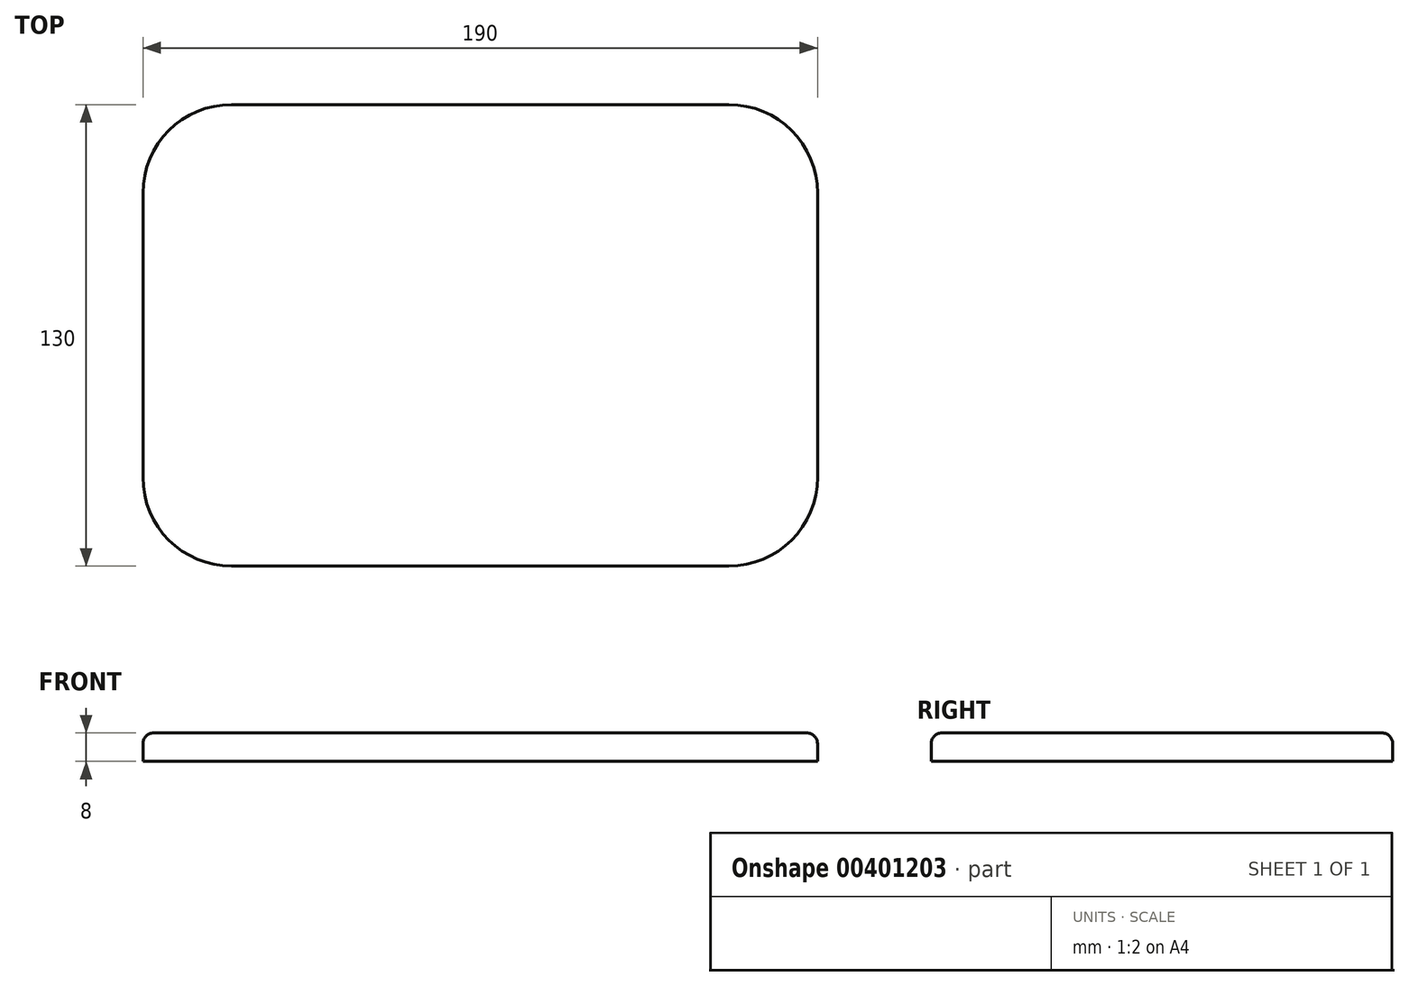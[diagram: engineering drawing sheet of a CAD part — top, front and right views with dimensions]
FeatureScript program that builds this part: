
annotation { "Feature Type Name" : "Feature", "Feature Type Description" : "" }
export const myFeature = defineFeature(function(context is Context, id is Id, definition is map)
    precondition{}
    {
        {
            var Q0;
            Q0=qCreatedBy(makeId("Top.planeOp"),FACE);
            var sketch = newSketch(context, id + "F0", { "sketchPlane" : qUnion([Q0])});
            skLineSegment(sketch, "E0.bottom", {"start": v(-95, 65) * mm, "end": v(95, 65) * mm});
            skLineSegment(sketch, "E0.top", {"start": v(-95, -65) * mm, "end": v(95, -65) * mm});
            skLineSegment(sketch, "E0.left", {"start": v(-95, 65) * mm, "end": v(-95, -65) * mm});
            skLineSegment(sketch, "E0.right", {"start": v(95, 65) * mm, "end": v(95, -65) * mm});
            skSolve(sketch);
        }
        {
            var Q0;
            Q0=makeQuery(id+"F0.imprint","IMPRINT",FACE,{"disambiguationData":[TD([[makeQuery(id+"F0.imprint","IMPRINT",EDGE,{"derivedFrom":sQuery(id+"F0.wireOp",EDGE,"E0.bottom")}),-1.0]])]});
            extrude(context, id + "F1", {"entities" : qUnion([Q0]), "depth" : 8 * mm});
        }
        {
            var Q0;
            Q0=makeQuery(id+"F1.opExtrude","SWEPT_EDGE",EDGE,{"disambiguationData":[OSD([sQuery(id+"F0.wireOp",EDGE,"E0.bottom"),sQuery(id+"F0.wireOp",EDGE,"E0.left")])]});
            var Q1;
            Q1=makeQuery(id+"F1.opExtrude","SWEPT_EDGE",EDGE,{"disambiguationData":[OSD([sQuery(id+"F0.wireOp",EDGE,"E0.top"),sQuery(id+"F0.wireOp",EDGE,"E0.left")])]});
            var Q2;
            Q2=makeQuery(id+"F1.opExtrude","SWEPT_EDGE",EDGE,{"disambiguationData":[OSD([sQuery(id+"F0.wireOp",EDGE,"E0.top"),sQuery(id+"F0.wireOp",EDGE,"E0.right")])]});
            var Q3;
            Q3=makeQuery(id+"F1.opExtrude","SWEPT_EDGE",EDGE,{"disambiguationData":[OSD([sQuery(id+"F0.wireOp",EDGE,"E0.bottom"),sQuery(id+"F0.wireOp",EDGE,"E0.right")])]});
            fillet(context, id + "F2", {"entities" : qUnion([Q0, Q1, Q2, Q3]), "radius" : 25 * mm, "tangentPropagation" : true, "allowEdgeOverflow" : false});
        }
        {
            var Q0;
            Q0=makeQuery(id+"F1.opExtrude","CAP_FACE",FACE,{"disambiguationData":[OSD([sQuery(id+"F0.wireOp",EDGE,"E0.bottom"),sQuery(id+"F0.wireOp",EDGE,"E0.top"),sQuery(id+"F0.wireOp",EDGE,"E0.left"),sQuery(id+"F0.wireOp",EDGE,"E0.right")])],"isStart":false});
            fillet(context, id + "F3", {"entities" : qUnion([Q0]), "radius" : 3 * mm, "tangentPropagation" : true, "allowEdgeOverflow" : false});
        }
    });
